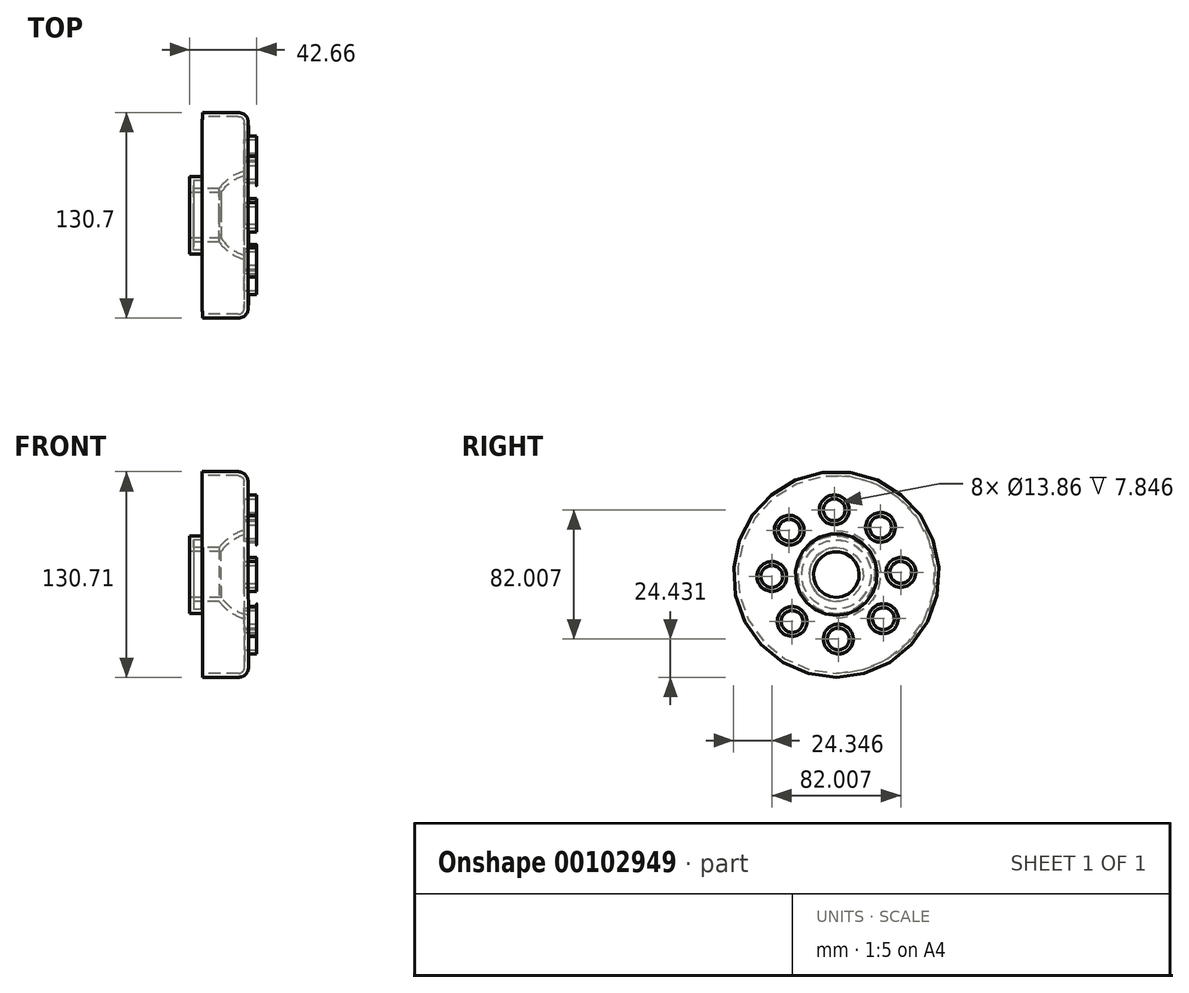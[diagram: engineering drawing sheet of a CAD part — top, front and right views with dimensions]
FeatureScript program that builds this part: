
annotation { "Feature Type Name" : "Feature", "Feature Type Description" : "" }
export const myFeature = defineFeature(function(context is Context, id is Id, definition is map)
    precondition{}
    {
        {
            var Q0;
            Q0=qCreatedBy(makeId("Front.planeOp"),FACE);
            var sketch = newSketch(context, id + "F0", { "sketchPlane" : qUnion([Q0])});
            skLineSegment(sketch, "E0", {"start": v(-0.7, 0.45) * mm, "end": v(-64.34, 0.29) * mm, "construction": true});
            skLineSegment(sketch, "E1.bottom", {"start": v(-34.45, 65.72) * mm, "end": v(-11.66, 65.72) * mm});
            skLineSegment(sketch, "E1.top", {"start": v(-42.4, 14.93) * mm, "end": v(-22.34, 14.93) * mm});
            skLineSegment(sketch, "E1.left", {"start": v(-42.4, 65.72) * mm, "end": v(-42.4, 65.72) * mm});
            skLineSegment(sketch, "E1.right", {"start": v(-5.3, 59.37) * mm, "end": v(-5.3, 26.4) * mm});
            skPoint(sketch, "E2.visualSharp", {"position": v(-5.3, 65.72) * mm});
            skArc(sketch, "E2.filletArc", {"start": v(-5.3, 59.37) * mm, "mid": v(-7.17, 63.86) * mm, "end": v(-11.66, 65.72) * mm});
            skPoint(sketch, "E3.visualSharp", {"position": v(-5.3, 14.93) * mm});
            skArc(sketch, "E4", {"start": v(-5.3, 26.4) * mm, "mid": v(-14.96, 22.37) * mm, "end": v(-22.34, 14.93) * mm});
            skLineSegment(sketch, "E5.top", {"start": v(-42.4, 24.95) * mm, "end": v(-34.45, 24.95) * mm});
            skLineSegment(sketch, "E5.right", {"start": v(-34.45, 65.72) * mm, "end": v(-34.45, 24.95) * mm});
            skLineSegment(sketch, "E6.trimOffspring", {"start": v(-42.4, 24.95) * mm, "end": v(-42.4, 14.93) * mm});
            skPoint(sketch, "E5.bottom.start.orphan", {"position": v(-42.4, 65.72) * mm});
            skSolve(sketch);
        }
        {
            var Q0;
            Q0 = qSketchRegion(id + "F0", true);
            var Q1;
            Q1=sQuery(id+"F0.wireOp",EDGE,"E0");
            revolve(context, id + "F1", {"entities" : qUnion([Q0]), "axis" : qUnion([Q1]), "revolveType" : RevolveType.FULL});
        }
        {
            var Q0;
            Q0=qCreatedBy(makeId("Right.planeOp"),FACE);
            var sketch = newSketch(context, id + "F2", { "sketchPlane" : qUnion([Q0])});
            skCircle(sketch, "E7", {"center": v(-1.29, 41.45) * mm, "radius": 9.47 * mm});
            skSolve(sketch);
        }
        {
            var Q0;
            Q0 = qSketchRegion(id + "F2", true);
            var Q1;
            Q1=makeQuery(id+"F1.opRevolve","SWEPT_FACE",FACE,{"disambiguationData":[OSD([sQuery(id+"F0.wireOp",EDGE,"E5.right")])]});
            extrude(context, id + "F3", {"entities" : qUnion([Q0]), "operationType" : NewBodyOperationType.ADD, "endBound" : BoundingType.UP_TO_SURFACE, "oppositeDirection" : true, "endBoundEntityFace" : qUnion([Q1]), "depth" : 25.4 * mm});
        }
        {
            var Q0;
            Q0=makeQuery(id+"F1.opRevolve","SWEPT_BODY",BODY,{"disambiguationData":[OSD([sQuery(id+"F0.wireOp",EDGE,"E1.bottom"),sQuery(id+"F0.wireOp",EDGE,"E1.top"),sQuery(id+"F0.wireOp",EDGE,"E1.left"),sQuery(id+"F0.wireOp",EDGE,"E1.right"),sQuery(id+"F0.wireOp",EDGE,"E2.filletArc"),sQuery(id+"F0.wireOp",EDGE,"E3.filletArc")])]});
            var Q1;
            Q1=makeQuery(id+"F1.opRevolve","SWEPT_FACE",FACE,{"disambiguationData":[OSD([sQuery(id+"F0.wireOp",EDGE,"E1.right")])]});
            circularPattern(context, id + "F4", {"operationType" : NewBodyOperationType.ADD, "entities" : qUnion([Q0]), "axis" : qUnion([Q1]), "angle" : 360 * degree, "instanceCount" : 8, "equalSpace" : true});
        }
        {
            var Q0;
            Q0=makeQuery(id+"F4.opPattern","COPY",FACE,{"derivedFrom":makeQuery(id+"F3.opExtrude","CAP_FACE",FACE,{"disambiguationData":[OSD([sQuery(id+"F2.wireOp",EDGE,"E7")])],"isStart":true}),"instanceName":"4"});
            var Q1;
            Q1=makeQuery(id+"F4.opPattern","COPY",FACE,{"derivedFrom":makeQuery(id+"F3.opExtrude","CAP_FACE",FACE,{"disambiguationData":[OSD([sQuery(id+"F2.wireOp",EDGE,"E7")])],"isStart":true}),"instanceName":"3"});
            var Q2;
            Q2=makeQuery(id+"F4.opPattern","COPY",FACE,{"derivedFrom":makeQuery(id+"F3.opExtrude","CAP_FACE",FACE,{"disambiguationData":[OSD([sQuery(id+"F2.wireOp",EDGE,"E7")])],"isStart":true}),"instanceName":"2"});
            var Q3;
            Q3=makeQuery(id+"F4.opPattern","COPY",FACE,{"derivedFrom":makeQuery(id+"F3.opExtrude","CAP_FACE",FACE,{"disambiguationData":[OSD([sQuery(id+"F2.wireOp",EDGE,"E7")])],"isStart":true}),"instanceName":"1"});
            var Q4;
            Q4=makeQuery(id+"F3.opExtrude","CAP_FACE",FACE,{"disambiguationData":[OSD([sQuery(id+"F2.wireOp",EDGE,"E7")])],"isStart":true});
            var Q5;
            Q5=makeQuery(id+"F4.opPattern","COPY",FACE,{"derivedFrom":makeQuery(id+"F3.opExtrude","CAP_FACE",FACE,{"disambiguationData":[OSD([sQuery(id+"F2.wireOp",EDGE,"E7")])],"isStart":true}),"instanceName":"7"});
            var Q6;
            Q6=makeQuery(id+"F4.opPattern","COPY",FACE,{"derivedFrom":makeQuery(id+"F3.opExtrude","CAP_FACE",FACE,{"disambiguationData":[OSD([sQuery(id+"F2.wireOp",EDGE,"E7")])],"isStart":true}),"instanceName":"6"});
            var Q7;
            Q7=makeQuery(id+"F4.opPattern","COPY",FACE,{"derivedFrom":makeQuery(id+"F3.opExtrude","CAP_FACE",FACE,{"disambiguationData":[OSD([sQuery(id+"F2.wireOp",EDGE,"E7")])],"isStart":true}),"instanceName":"5"});
            var Q8;
            Q8=makeQuery(id+"F1.opRevolve","SWEPT_FACE",FACE,{"disambiguationData":[OSD([sQuery(id+"F0.wireOp",EDGE,"E5.right")])]});
            shell(context, id + "F5", {"entities" : qUnion([Q0, Q1, Q2, Q3, Q4, Q5, Q6, Q7, Q8]), "thickness" : 2.54 * mm});
        }
    });
